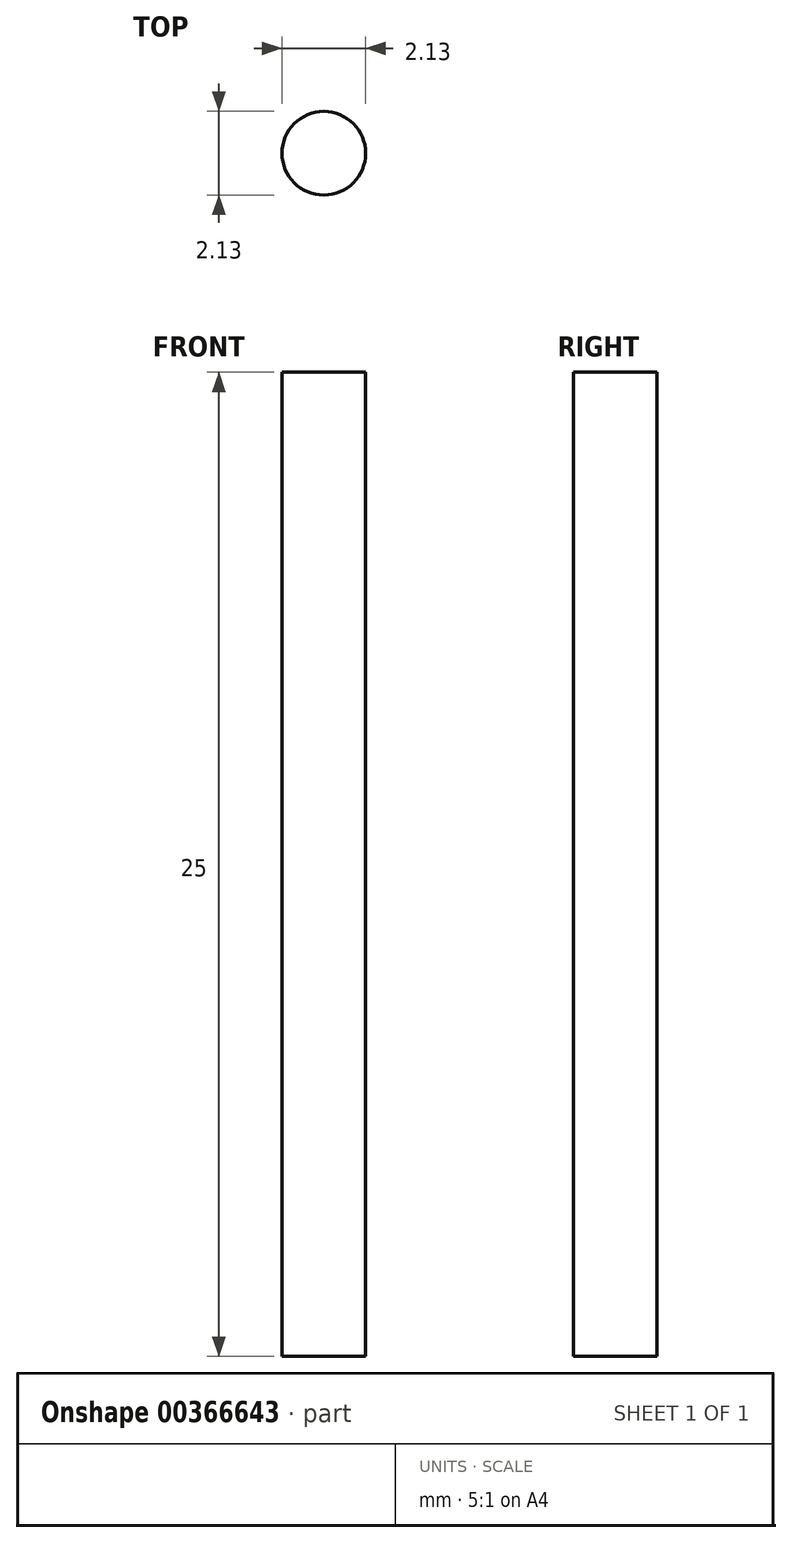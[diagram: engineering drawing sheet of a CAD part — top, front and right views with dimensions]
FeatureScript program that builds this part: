
annotation { "Feature Type Name" : "Feature", "Feature Type Description" : "" }
export const myFeature = defineFeature(function(context is Context, id is Id, definition is map)
    precondition{}
    {
        {
            var Q0;
            Q0=qCreatedBy(makeId("Top.planeOp"),FACE);
            var sketch = newSketch(context, id + "F0", { "sketchPlane" : qUnion([Q0])});
            skCircle(sketch, "E0", {"center": v(-56.57, -20.22) * mm, "radius": 1.06 * mm});
            skSolve(sketch);
        }
        {
            var Q0;
            Q0=makeQuery(id+"F0.imprint","IMPRINT",FACE,{"disambiguationData":[TD([[makeQuery(id+"F0.imprint","IMPRINT",EDGE,{"derivedFrom":sQuery(id+"F0.wireOp",EDGE,"E0")}),1.0]])]});
            extrude(context, id + "F1", {"entities" : qUnion([Q0]), "depth" : 25 * mm});
        }
    });
